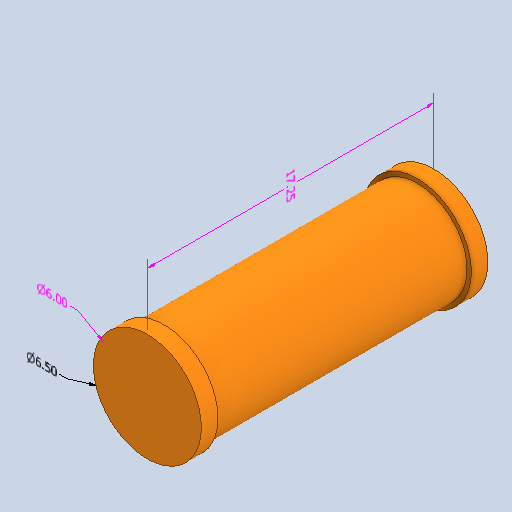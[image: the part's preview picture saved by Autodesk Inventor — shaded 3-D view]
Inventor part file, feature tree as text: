
AUTODESK INVENTOR PART (.ipt)
format: ipt  version: 2022 (Build 260153070, 153G)  size: 138,752 bytes
history: native  units: in
note: dims shown in document units (in); Inventor stores cm internally (conversion verified against a paired STEP export)
features: other x4, extrude x4, sketch x4
ambient origin geometry x8: Origin, YZ Plane, XZ Plane, XY Plane, X Axis, Y Axis, Z Axis, Center Point
bodies: Solid1 (feature_tree)
feature tree (12):
  other  "Annotations"
  extrude  "Extrusion1"  Depth=5.75in
  extrude  "Extrusion2"  Depth=16.0in
  extrude  "Extrusion3"  Depth=1.0in TaperAngle=0.0deg
  extrude  "Extrusion4"  [1 undecoded]
  sketch  "Sketch1"  dims[d2=0.0in d6=5.75in]
  sketch  "Sketch2"  dims[d7=16.0in d8=0.0in d9=6.5in]
  sketch  "Sketch3"  dims[d10=1.0in d11=0.0in d12=1.0in d13=0.0in]
  sketch  "Sketch4"  dims[d14=1.3544in d15=6.5in d3=1.032in d4=6.0in d5=17.25in]
  other  "Diameter Dimension 1"
  other  "Linear Dimension 1"
  other  "Diameter Dimension 2"
note: 1 required parameter value undecoded (feature->parameter linkage not recoverable at this tier; creation-order binding heuristic only, values carry confidence <= 0.55)
